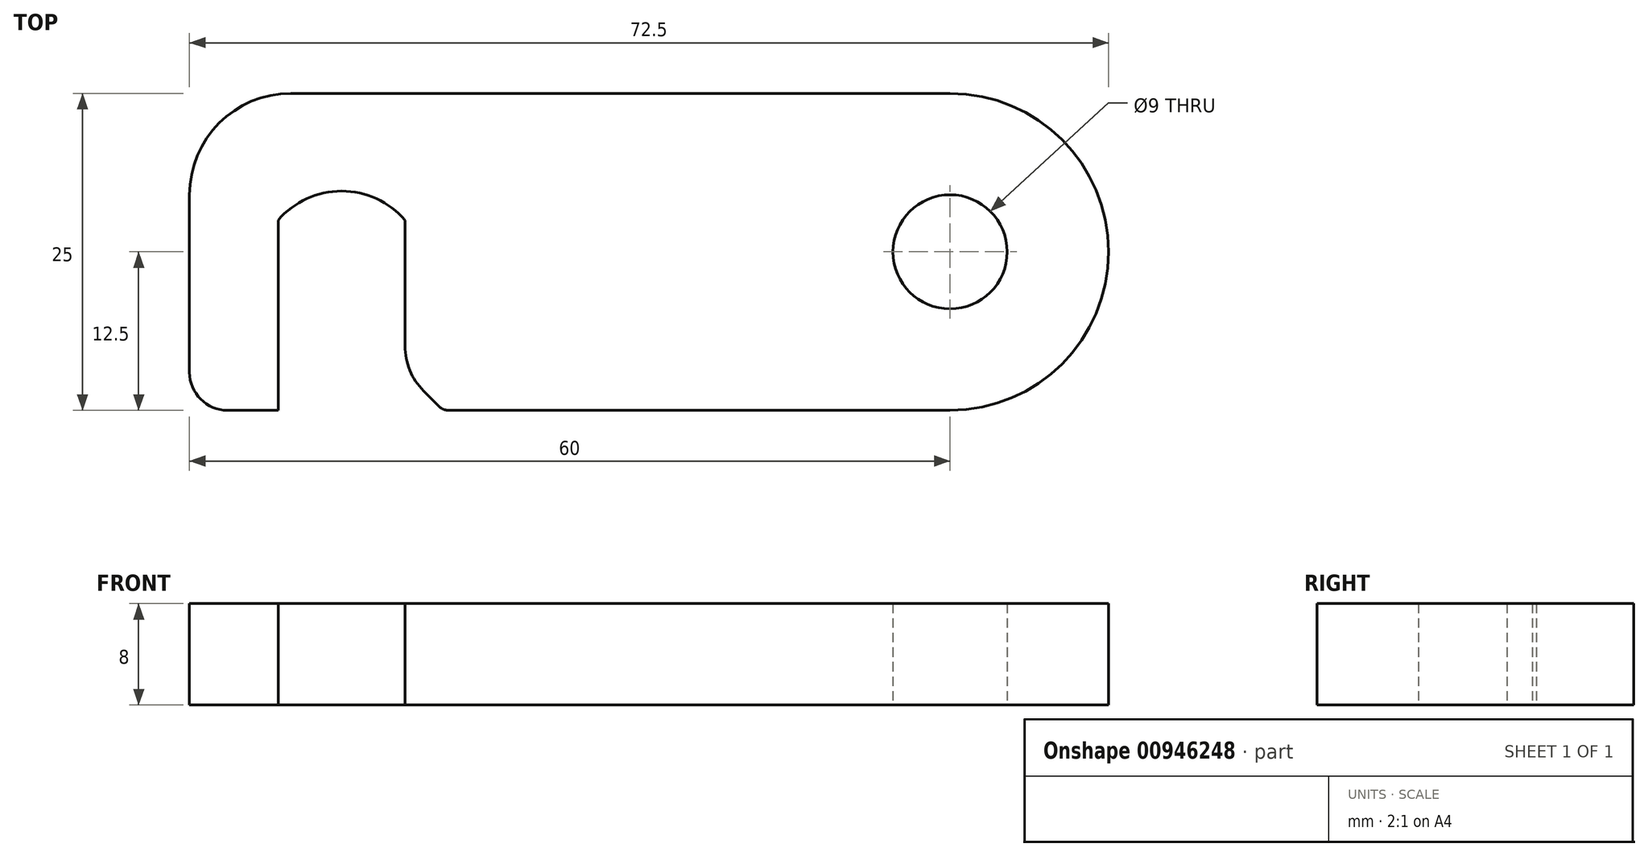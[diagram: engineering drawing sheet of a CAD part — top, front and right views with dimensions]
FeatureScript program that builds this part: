
annotation { "Feature Type Name" : "Feature", "Feature Type Description" : "" }
export const myFeature = defineFeature(function(context is Context, id is Id, definition is map)
    precondition{}
    {
        {
            var Q0;
            Q0=qCreatedBy(makeId("Top.planeOp"),FACE);
            var sketch = newSketch(context, id + "F0", { "sketchPlane" : qUnion([Q0])});
            skCircle(sketch, "E0", {"center": v(0, 0) * mm, "radius": 4.5 * mm});
            skCircle(sketch, "E1", {"center": v(0, 0) * mm, "radius": 12.5 * mm});
            skLineSegment(sketch, "E2", {"start": v(-52, 12.5) * mm, "end": v(0, 12.5) * mm});
            skLineSegment(sketch, "E3", {"start": v(0, 0) * mm, "end": v(-29.49, 0) * mm, "construction": true});
            skLineSegment(sketch, "E4.MirrorCS", {"start": v(-60, -12.5) * mm, "end": v(0, -12.5) * mm});
            skLineSegment(sketch, "E5", {"start": v(-60, 4.5) * mm, "end": v(-60, -12.5) * mm});
            skPoint(sketch, "E6.visualSharp", {"position": v(-60, 12.5) * mm});
            skArc(sketch, "E6.filletArc", {"start": v(-52, 12.5) * mm, "mid": v(-57.66, 10.16) * mm, "end": v(-60, 4.5) * mm});
            skLineSegment(sketch, "E7", {"start": v(-53, 2.5) * mm, "end": v(-53, -12.5) * mm});
            skLineSegment(sketch, "E8.0", {"start": v(-43, 2.5) * mm, "end": v(-43, -12.5) * mm});
            skArc(sketch, "E9", {"start": v(-43, 2.5) * mm, "mid": v(-48, 4.8) * mm, "end": v(-53, 2.5) * mm});
            skSolve(sketch);
        }
        {
            var Q0;
            Q0=makeQuery(id+"F0.imprint","IMPRINT",FACE,{"disambiguationData":[TD([[makeQuery(id+"F0.imprint","IMPRINT",EDGE,{"derivedFrom":sQuery(id+"F0.wireOp",EDGE,"E0")}),-1.0]])]});
            var Q1;
            {var subQ3=sQuery(id+"F0.wireOp",EDGE,"E2");Q1=makeQuery(id+"F0.imprint","IMPRINT",FACE,{"disambiguationData":[TD([[makeQuery(id+"F0.imprint","IMPRINT",EDGE,{"derivedFrom":subQ3}),-1.0]])]});}
            extrude(context, id + "F1", {"entities" : qUnion([Q0, Q1]), "depth" : 8 * mm, "offsetDistance" : 25 * mm});
        }
        {
            var Q0;
            Q0=makeQuery(id+"F1.opExtrude","SWEPT_EDGE",EDGE,{"disambiguationData":[OSD([sQuery(id+"F0.wireOp",EDGE,"E4.MirrorCS"),sQuery(id+"F0.wireOp",EDGE,"E8.0")])]});
            chamfer(context, id + "F2", {"entities" : qUnion([Q0]), "width" : 3 * mm, "tangentPropagation" : true});
        }
        {
            var Q0;
            {var subQ0=sQuery(id+"F0.wireOp",EDGE,"E8.0");Q0=makeQuery(id+"F2.opChamfer","BLEND_EDGE",EDGE,{"blendedFrom":[makeQuery(id+"F1.opExtrude","SWEPT_EDGE",EDGE,{"disambiguationData":[OSD([sQuery(id+"F0.wireOp",EDGE,"E4.MirrorCS"),subQ0])]}),makeQuery(id+"F1.opExtrude","SWEPT_FACE",FACE,{"disambiguationData":[OSD([subQ0])]})],"blendedInto":[makeQuery(id+"F1.opExtrude","SWEPT_FACE",FACE,{"disambiguationData":[OSD([subQ0])]})]});}
            fillet(context, id + "F3", {"entities" : qUnion([Q0]), "radius" : 5 * mm, "tangentPropagation" : true, "allowEdgeOverflow" : false});
        }
        {
            var Q0;
            {var subQ0=sQuery(id+"F0.wireOp",EDGE,"E4.MirrorCS");var subQ1=sQuery(id+"F0.wireOp",EDGE,"E8.0");Q0=makeQuery(id+"F2.opChamfer","BLEND_EDGE",EDGE,{"blendedFrom":[makeQuery(id+"F1.opExtrude","SWEPT_EDGE",EDGE,{"disambiguationData":[OSD([subQ0,subQ1])]}),makeQuery(id+"F1.opExtrude","SWEPT_FACE",FACE,{"disambiguationData":[OSD([subQ0]),TDD([makeQuery(id+"F0.imprint","IMPRINT",EDGE,{"disambiguationData":[TD([[makeQuery(id+"F0.imprint","INTERSECT",VERTEX,{"derivedFrom":[sQuery(id+"F0.wireOp",EDGE,"E1"),subQ0]}),1.0]])],"derivedFrom":subQ0})])]})],"blendedInto":[makeQuery(id+"F1.opExtrude","SWEPT_FACE",FACE,{"disambiguationData":[OSD([subQ0]),TDD([makeQuery(id+"F0.imprint","IMPRINT",EDGE,{"disambiguationData":[TD([[makeQuery(id+"F0.imprint","INTERSECT",VERTEX,{"derivedFrom":[sQuery(id+"F0.wireOp",EDGE,"E1"),subQ0]}),1.0]])],"derivedFrom":subQ0})])]})]});}
            fillet(context, id + "F4", {"entities" : qUnion([Q0]), "radius" : 1 * mm, "tangentPropagation" : true, "allowEdgeOverflow" : false});
        }
        {
            var Q0;
            Q0=makeQuery(id+"F1.opExtrude","SWEPT_EDGE",EDGE,{"disambiguationData":[OSD([sQuery(id+"F0.wireOp",EDGE,"E4.MirrorCS"),sQuery(id+"F0.wireOp",EDGE,"E5")])]});
            fillet(context, id + "F5", {"entities" : qUnion([Q0]), "radius" : 3 * mm, "tangentPropagation" : true, "allowEdgeOverflow" : false});
        }
    });
